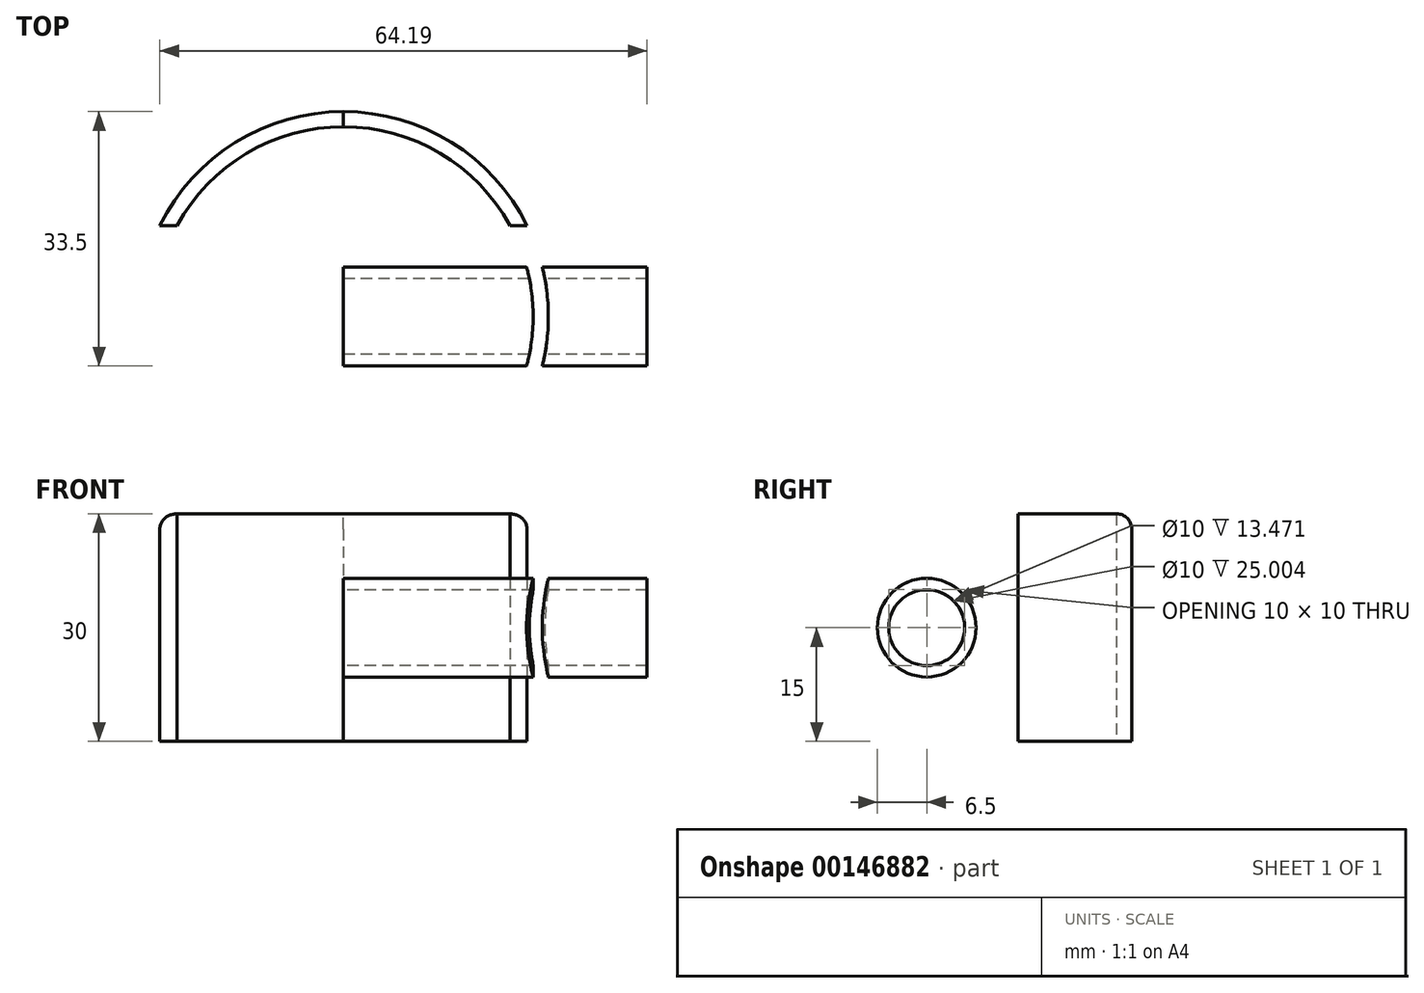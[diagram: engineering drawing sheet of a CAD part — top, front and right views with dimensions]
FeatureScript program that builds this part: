
annotation { "Feature Type Name" : "Feature", "Feature Type Description" : "" }
export const myFeature = defineFeature(function(context is Context, id is Id, definition is map)
    precondition{}
    {
        {
            var Q0;
            Q0=qCreatedBy(makeId("Top.planeOp"),FACE);
            var sketch = newSketch(context, id + "F0", { "sketchPlane" : qUnion([Q0])});
            skCircle(sketch, "E0", {"center": v(0, 0) * mm, "radius": 25 * mm});
            skLineSegment(sketch, "E1", {"start": v(0, 0) * mm, "end": v(0, -25) * mm});
            skLineSegment(sketch, "E2", {"start": v(0, -25) * mm, "end": v(0, 25) * mm});
            skCircle(sketch, "E3", {"center": v(0, 0) * mm, "radius": 27 * mm});
            skLineSegment(sketch, "E4", {"start": v(0, 25) * mm, "end": v(0, 27) * mm});
            skLineSegment(sketch, "E5", {"start": v(0, 27) * mm, "end": v(0, -27) * mm});
            skLineSegment(sketch, "E6", {"start": v(0, 27) * mm, "end": v(0, 12) * mm});
            skLineSegment(sketch, "E7", {"start": v(0, 12) * mm, "end": v(24.19, 12) * mm});
            skLineSegment(sketch, "E8", {"start": v(24.19, 12) * mm, "end": v(-24.19, 12) * mm});
            skSolve(sketch);
        }
        {
            var Q0;
            {var subQ0=sQuery(id+"F0.wireOp",EDGE,"E8");var subQ1=sQuery(id+"F0.wireOp",EDGE,"E0");var subQ2=makeQuery(id+"F0.imprint","INTERSECT",VERTEX,{"disambiguationData":[OD(0.0)],"derivedFrom":[subQ1,subQ0]});Q0=makeQuery(id+"F0.imprint","IMPRINT",FACE,{"disambiguationData":[TD([[makeQuery(id+"F0.imprint","IMPRINT",EDGE,{"disambiguationData":[TD([[subQ2,1.0]])],"derivedFrom":subQ1}),-1.0]])]});}
            extrude(context, id + "F1", {"entities" : qUnion([Q0]), "depth" : 30 * mm});
        }
        {
            var Q0;
            Q0=qCreatedBy(makeId("Right.planeOp"),FACE);
            var sketch = newSketch(context, id + "F2", { "sketchPlane" : qUnion([Q0])});
            skLineSegment(sketch, "E9", {"start": v(0, 0) * mm, "end": v(0, 15) * mm});
            skCircle(sketch, "E10", {"center": v(0, 15) * mm, "radius": 5 * mm});
            skCircle(sketch, "E11", {"center": v(0, 15) * mm, "radius": 6.5 * mm});
            skSolve(sketch);
        }
        {
            var Q0;
            Q0=makeQuery(id+"F2.imprint","IMPRINT",FACE,{"disambiguationData":[TD([[makeQuery(id+"F2.imprint","IMPRINT",EDGE,{"derivedFrom":sQuery(id+"F2.wireOp",EDGE,"E10")}),-1.0]])]});
            extrude(context, id + "F3", {"entities" : qUnion([Q0]), "operationType" : NewBodyOperationType.ADD, "depth" : 40 * mm});
        }
        {
            var Q0;
            {var subQ0=sQuery(id+"F0.wireOp",EDGE,"E2");var subQ4=makeQuery(id+"F0.imprint","IMPRINT",VERTEX,{"derivedFrom":subQ0});Q0=makeQuery(id+"F0.imprint","IMPRINT",FACE,{"disambiguationData":[TD([[makeQuery(id+"F0.imprint","IMPRINT",EDGE,{"disambiguationData":[TD([[subQ4,1.0]])],"derivedFrom":subQ0}),-1.0]])]});}
            var Q1;
            {var subQ0=sQuery(id+"F0.wireOp",EDGE,"E5");var subQ4=makeQuery(id+"F0.imprint","IMPRINT",VERTEX,{"derivedFrom":subQ0});Q1=makeQuery(id+"F0.imprint","IMPRINT",FACE,{"disambiguationData":[TD([[makeQuery(id+"F0.imprint","IMPRINT",EDGE,{"disambiguationData":[TD([[subQ4,1.0]])],"derivedFrom":subQ0}),1.0]])]});}
            extrude(context, id + "F4", {"entities" : qUnion([Q0, Q1]), "operationType" : NewBodyOperationType.REMOVE, "depth" : 25 * mm});
        }
        {
            var Q0;
            Q0=makeQuery(id+"F2.imprint","IMPRINT",FACE,{"disambiguationData":[TD([[makeQuery(id+"F2.imprint","IMPRINT",EDGE,{"derivedFrom":sQuery(id+"F2.wireOp",EDGE,"E10")}),1.0]])]});
            extrude(context, id + "F5", {"entities" : qUnion([Q0]), "operationType" : NewBodyOperationType.REMOVE, "depth" : 30 * mm});
        }
        {
            var Q0;
            Q0=makeQuery(id+"F1.opExtrude","SWEPT_BODY",BODY,{"disambiguationData":[OSD([sQuery(id+"F0.wireOp",EDGE,"E0"),sQuery(id+"F0.wireOp",EDGE,"E3"),sQuery(id+"F0.wireOp",EDGE,"E5")])]});
            var Q1;
            Q1=qCreatedBy(makeId("Right.planeOp"),FACE);
            mirror(context, id + "F6", {"operationType" : NewBodyOperationType.ADD, "entities" : qUnion([Q0]), "mirrorPlane" : qUnion([Q1])});
        }
        {
            var Q0;
            {var subQ0=makeQuery(id+"F1.opExtrude","CAP_EDGE",EDGE,{"disambiguationData":[OSD([sQuery(id+"F0.wireOp",EDGE,"E3")])],"isStart":false});Q0=makeQuery(id+"F6.boolean.opBoolean","MERGE",EDGE,{"derivedFrom":[subQ0,makeQuery(id+"F6.opPattern","COPY",EDGE,{"derivedFrom":subQ0,"instanceName":"1"})]});}
            fillet(context, id + "F7", {"entities" : qUnion([Q0]), "radius" : 2 * mm, "tangentPropagation" : true, "allowEdgeOverflow" : false});
        }
    });
